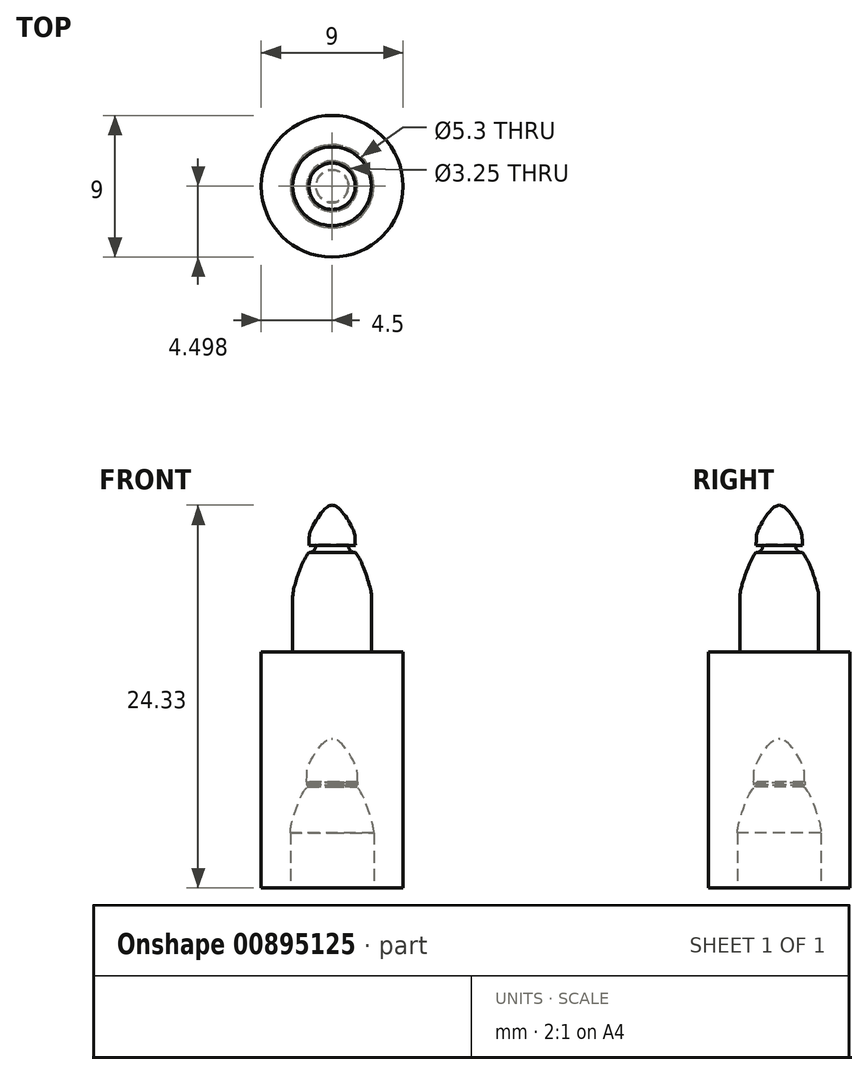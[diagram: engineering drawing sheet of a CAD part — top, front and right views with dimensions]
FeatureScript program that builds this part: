
annotation { "Feature Type Name" : "Feature", "Feature Type Description" : "" }
export const myFeature = defineFeature(function(context is Context, id is Id, definition is map)
    precondition{}
    {
        {
            var Q0;
            Q0=qCreatedBy(makeId("Top.planeOp"),FACE);
            var sketch = newSketch(context, id + "F0", { "sketchPlane" : qUnion([Q0])});
            skCircle(sketch, "E0", {"center": v(0, 0) * mm, "radius": 4.5 * mm});
            skSolve(sketch);
        }
        {
            var Q0;
            Q0 = qSketchRegion(id + "F0", true);
            extrude(context, id + "F1", {"entities" : qUnion([Q0]), "depth" : 15 * mm, "offsetDistance" : 25 * mm});
        }
        {
            var Q0;
            Q0=qCreatedBy(makeId("Front.planeOp"),FACE);
            var sketch = newSketch(context, id + "F2", { "sketchPlane" : qUnion([Q0])});
            skLineSegment(sketch, "E1.0", {"start": v(-4.5, 15) * mm, "end": v(4.5, 15) * mm});
            skLineSegment(sketch, "E2", {"start": v(-2.5, 15) * mm, "end": v(-2.5, 17.02) * mm});
            skLineSegment(sketch, "E3", {"start": v(0, 24.33) * mm, "end": v(0, 15) * mm});
            skLineSegment(sketch, "E4", {"start": v(-2.5, 17.02) * mm, "end": v(-2.5, 18.5) * mm});
            skLineSegment(sketch, "E5.MirrorCS", {"start": v(2.5, 17.02) * mm, "end": v(2.5, 18.5) * mm});
            skLineSegment(sketch, "E6.MirrorCS", {"start": v(2.5, 15) * mm, "end": v(2.5, 17.02) * mm});
            skFitSpline(sketch, "E7", {"points": [v(-1.47, 21.75) * mm, v(-1.37, 22.66) * mm, v(-0.4, 24.14) * mm, v(0, 24.33) * mm], "startDerivative": vector(0.35, 4.2) * mm, "endDerivative": vector(1.73, 0.48) * mm});
            skArc(sketch, "E8", {"start": v(-1.05, 21.84) * mm, "mid": v(-1.13, 21.47) * mm, "end": v(-1.47, 21.31) * mm});
            skLineSegment(sketch, "E9", {"start": v(-1.05, 21.84) * mm, "end": v(-1.47, 21.75) * mm});
            skFitSpline(sketch, "E10", {"points": [v(-1.47, 21.31) * mm, v(-1.98, 20.4) * mm, v(-2.47, 18.84) * mm, v(-2.5, 18.5) * mm], "startDerivative": vector(-1.6, -1.8) * mm, "endDerivative": vector(-0.02, -1.24) * mm});
            skFitSpline(sketch, "E11.0", {"points": [v(-1.62, 21.76) * mm, v(-1.6, 21.93) * mm, v(-1.6, 22.18) * mm, v(-1.6, 22.43) * mm, v(-1.54, 22.67) * mm, v(-1.42, 22.95) * mm, v(-1.2, 23.35) * mm, v(-0.88, 23.84) * mm, v(-0.6, 24.16) * mm, v(-0.41, 24.33) * mm, v(-0.27, 24.4) * mm, v(-0.14, 24.45) * mm, v(-0.07, 24.47) * mm, v(-0.04, 24.47) * mm]});
            skArc(sketch, "E12.0", {"start": v(-1.44, 21.67) * mm, "mid": v(-1.45, 21.59) * mm, "end": v(-1.48, 21.5) * mm});
            skLineSegment(sketch, "E13", {"start": v(-1.62, 21.76) * mm, "end": v(-1.62, 21.55) * mm});
            skLineSegment(sketch, "E14", {"start": v(-1.62, 21.55) * mm, "end": v(-1.44, 21.67) * mm});
            skFitSpline(sketch, "E15.0", {"points": [v(-1.58, 21.41) * mm, v(-1.66, 21.33) * mm, v(-1.8, 21.15) * mm, v(-1.98, 20.81) * mm, v(-2.15, 20.4) * mm, v(-2.33, 19.9) * mm, v(-2.48, 19.41) * mm, v(-2.58, 19.05) * mm, v(-2.62, 18.83) * mm, v(-2.65, 18.65) * mm, v(-2.65, 18.56) * mm, v(-2.65, 18.51) * mm]});
            skLineSegment(sketch, "E16", {"start": v(-1.58, 21.41) * mm, "end": v(-1.48, 21.5) * mm});
            skPoint(sketch, "E17.endSnap0", {"position": v(-1.53, 21.6) * mm});
            skLineSegment(sketch, "E18", {"start": v(-2.65, 18.51) * mm, "end": v(-2.65, 15) * mm});
            skFitSpline(sketch, "E19", {"points": [v(-0.04, 24.47) * mm, v(0, 24.48) * mm], "startDerivative": vector(0.04, 0) * mm, "endDerivative": vector(0.04, 0) * mm});
            skSolve(sketch);
        }
        {
            var Q0;
            Q0=qCreatedBy(makeId("Right.planeOp"),FACE);
            var sketch = newSketch(context, id + "F3", { "sketchPlane" : qUnion([Q0])});
            skLineSegment(sketch, "E20.0", {"start": v(-4.5, 0) * mm, "end": v(4.5, 0) * mm});
            skLineSegment(sketch, "E21", {"start": v(-4.5, 0) * mm, "end": v(-4.5, 15) * mm});
            skLineSegment(sketch, "E22", {"start": v(4.5, 15) * mm, "end": v(4.5, 0) * mm});
            skLineSegment(sketch, "E23.0", {"start": v(-3.5, 0) * mm, "end": v(3.5, 0) * mm});
            skLineSegment(sketch, "E24.MirrorCS", {"start": v(0, 9.33) * mm, "end": v(0, 0) * mm});
            skFitSpline(sketch, "E25.0", {"points": [v(-1.62, 6.76) * mm, v(-1.61, 6.93) * mm, v(-1.6, 7.18) * mm, v(-1.6, 7.43) * mm, v(-1.54, 7.67) * mm, v(-1.42, 7.95) * mm, v(-1.2, 8.35) * mm, v(-0.88, 8.84) * mm, v(-0.61, 9.16) * mm, v(-0.41, 9.33) * mm, v(-0.27, 9.4) * mm, v(-0.15, 9.45) * mm, v(-0.08, 9.47) * mm, v(-0.04, 9.47) * mm]});
            skArc(sketch, "E26.0", {"start": v(-1.45, 6.67) * mm, "mid": v(-1.45, 6.59) * mm, "end": v(-1.48, 6.5) * mm});
            skLineSegment(sketch, "E27", {"start": v(-1.62, 6.76) * mm, "end": v(-1.62, 6.55) * mm});
            skLineSegment(sketch, "E28", {"start": v(-1.62, 6.55) * mm, "end": v(-1.45, 6.67) * mm});
            skFitSpline(sketch, "E29.0", {"points": [v(-1.59, 6.41) * mm, v(-1.66, 6.33) * mm, v(-1.8, 6.15) * mm, v(-1.98, 5.81) * mm, v(-2.15, 5.4) * mm, v(-2.33, 4.9) * mm, v(-2.48, 4.41) * mm, v(-2.58, 4.05) * mm, v(-2.63, 3.83) * mm, v(-2.65, 3.65) * mm, v(-2.65, 3.56) * mm, v(-2.65, 3.51) * mm]});
            skLineSegment(sketch, "E30", {"start": v(-1.59, 6.41) * mm, "end": v(-1.48, 6.5) * mm});
            skPoint(sketch, "E31.endSnap0", {"position": v(-1.54, 6.6) * mm});
            skLineSegment(sketch, "E32", {"start": v(-2.65, 3.51) * mm, "end": v(-2.65, 0) * mm});
            skFitSpline(sketch, "E33", {"points": [v(-0.04, 9.47) * mm, v(0, 9.48) * mm], "startDerivative": vector(0.04, 0) * mm, "endDerivative": vector(0.04, 0) * mm});
            skLineSegment(sketch, "E34", {"start": v(0, 9.33) * mm, "end": v(0, 9.48) * mm});
            skSolve(sketch);
        }
        {
            var Q0;
            {var subQ1=sQuery(id+"F2.wireOp",EDGE,"E2");Q0=makeQuery(id+"F2.imprint","IMPRINT",FACE,{"disambiguationData":[TD([[makeQuery(id+"F2.imprint","IMPRINT",EDGE,{"derivedFrom":subQ1}),-1.0]])]});}
            var Q1;
            Q1=sQuery(id+"F2.wireOp",EDGE,"E3");
            var Q2;
            Q2=sQuery(id+"F2.wireOp",EDGE,"E3");
            revolve(context, id + "F4", {"operationType" : NewBodyOperationType.ADD, "surfaceOperationType" : NewSurfaceOperationType.NEW, "entities" : qUnion([Q0]), "surfaceEntities" : qUnion([Q1]), "axis" : qUnion([Q2]), "revolveType" : RevolveType.FULL});
        }
        {
            var Q0;
            Q0 = qSketchRegion(id + "F3", true);
            var Q1;
            Q1=sQuery(id+"F3.wireOp",EDGE,"E24.MirrorCS");
            revolve(context, id + "F5", {"operationType" : NewBodyOperationType.REMOVE, "surfaceOperationType" : NewSurfaceOperationType.NEW, "entities" : qUnion([Q0]), "axis" : qUnion([Q1]), "revolveType" : RevolveType.FULL, "oppositeDirection" : true});
        }
    });
